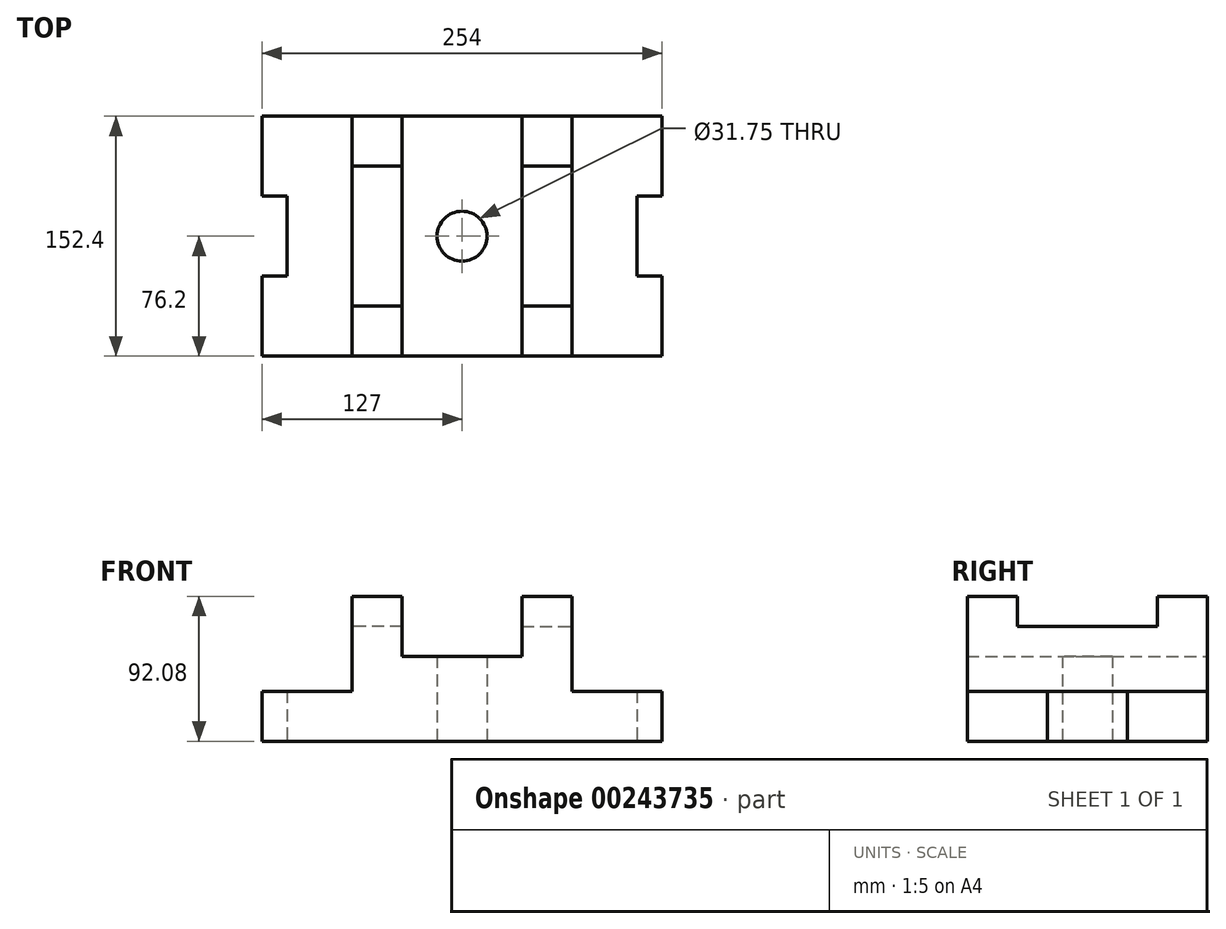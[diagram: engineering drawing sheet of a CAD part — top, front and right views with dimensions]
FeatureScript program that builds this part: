
annotation { "Feature Type Name" : "Feature", "Feature Type Description" : "" }
export const myFeature = defineFeature(function(context is Context, id is Id, definition is map)
    precondition{}
    {
        {
            var Q0;
            Q0=qCreatedBy(makeId("Top.planeOp"),FACE);
            var sketch = newSketch(context, id + "F0", { "sketchPlane" : qUnion([Q0])});
            skLineSegment(sketch, "E0", {"start": v(0, 0) * mm, "end": v(-127, 0) * mm});
            skLineSegment(sketch, "E1", {"start": v(0, 0) * mm, "end": v(0, 50.8) * mm});
            skLineSegment(sketch, "E2", {"start": v(-15.88, 50.8) * mm, "end": v(-15.88, 101.6) * mm});
            skLineSegment(sketch, "E3", {"start": v(-15.87, 101.6) * mm, "end": v(0, 101.6) * mm});
            skLineSegment(sketch, "E4", {"start": v(0, 50.8) * mm, "end": v(-15.88, 50.8) * mm});
            skLineSegment(sketch, "E5", {"start": v(0, 101.6) * mm, "end": v(0, 152.4) * mm});
            skLineSegment(sketch, "E6", {"start": v(0, 152.4) * mm, "end": v(-57.15, 152.4) * mm});
            skLineSegment(sketch, "E7", {"start": v(-57.15, 152.4) * mm, "end": v(-88.9, 152.4) * mm});
            skLineSegment(sketch, "E8", {"start": v(-88.9, 152.4) * mm, "end": v(-127, 152.4) * mm});
            skLineSegment(sketch, "E9", {"start": v(0, 0) * mm, "end": v(-57.15, 0) * mm});
            skLineSegment(sketch, "E10", {"start": v(-57.15, 152.4) * mm, "end": v(-57.15, 0) * mm});
            skLineSegment(sketch, "E11", {"start": v(-88.9, 120.65) * mm, "end": v(-57.15, 120.65) * mm});
            skLineSegment(sketch, "E12", {"start": v(-88.9, 0) * mm, "end": v(-88.9, 31.75) * mm});
            skLineSegment(sketch, "E13", {"start": v(-88.9, 31.75) * mm, "end": v(-57.15, 31.75) * mm});
            skLineSegment(sketch, "E14", {"start": v(-88.9, 152.4) * mm, "end": v(-88.9, 120.65) * mm});
            skLineSegment(sketch, "E15", {"start": v(-88.9, 120.65) * mm, "end": v(-88.9, 31.75) * mm});
            skLineSegment(sketch, "E16", {"start": v(-127, 152.4) * mm, "end": v(-127, 0) * mm});
            skLineSegment(sketch, "E17.MirrorCS", {"start": v(-165.1, 152.4) * mm, "end": v(-127, 152.4) * mm});
            skLineSegment(sketch, "E18.MirrorCS", {"start": v(-165.1, 152.4) * mm, "end": v(-165.1, 120.65) * mm});
            skLineSegment(sketch, "E19.MirrorCS", {"start": v(-196.85, 152.4) * mm, "end": v(-196.85, 0) * mm});
            skLineSegment(sketch, "E20.MirrorCS", {"start": v(-165.1, 120.65) * mm, "end": v(-165.1, 31.75) * mm});
            skLineSegment(sketch, "E21.MirrorCS", {"start": v(-254, 0) * mm, "end": v(-127, 0) * mm});
            skLineSegment(sketch, "E22.MirrorCS", {"start": v(-165.1, 0) * mm, "end": v(-165.1, 31.75) * mm});
            skLineSegment(sketch, "E23.MirrorCS", {"start": v(-196.85, 152.4) * mm, "end": v(-165.1, 152.4) * mm});
            skLineSegment(sketch, "E24.MirrorCS", {"start": v(-254, 152.4) * mm, "end": v(-196.85, 152.4) * mm});
            skLineSegment(sketch, "E25.MirrorCS", {"start": v(-254, 101.6) * mm, "end": v(-254, 152.4) * mm});
            skLineSegment(sketch, "E26.MirrorCS", {"start": v(-238.12, 50.8) * mm, "end": v(-238.12, 101.6) * mm});
            skLineSegment(sketch, "E27.MirrorCS", {"start": v(-254, 50.8) * mm, "end": v(-238.12, 50.8) * mm});
            skLineSegment(sketch, "E28.MirrorCS", {"start": v(-238.13, 101.6) * mm, "end": v(-254, 101.6) * mm});
            skLineSegment(sketch, "E29.MirrorCS", {"start": v(-254, 0) * mm, "end": v(-254, 50.8) * mm});
            skLineSegment(sketch, "E30.MirrorCS", {"start": v(-165.1, 120.65) * mm, "end": v(-196.85, 120.65) * mm});
            skLineSegment(sketch, "E31.MirrorCS", {"start": v(-165.1, 31.75) * mm, "end": v(-196.85, 31.75) * mm});
            skCircle(sketch, "E32", {"center": v(-127, 76.2) * mm, "radius": 15.88 * mm});
            skSolve(sketch);
        }
        {
            var Q0;
            Q0=makeQuery(id+"F0.imprint","IMPRINT",FACE,{"disambiguationData":[TD([[makeQuery(id+"F0.imprint","IMPRINT",EDGE,{"derivedFrom":sQuery(id+"F0.wireOp",EDGE,"E1")}),1.0]])]});
            extrude(context, id + "F1", {"entities" : qUnion([Q0]), "depth" : 31.75 * mm});
        }
        {
            var Q0;
            {var subQ0=sQuery(id+"F0.wireOp",EDGE,"E7");Q0=makeQuery(id+"F0.imprint","IMPRINT",FACE,{"disambiguationData":[TD([[makeQuery(id+"F0.imprint","IMPRINT",EDGE,{"derivedFrom":subQ0}),1.0]])]});}
            var Q1;
            {var subQ3=sQuery(id+"F0.wireOp",EDGE,"E12");Q1=makeQuery(id+"F0.imprint","IMPRINT",FACE,{"disambiguationData":[TD([[makeQuery(id+"F0.imprint","IMPRINT",EDGE,{"derivedFrom":subQ3}),-1.0]])]});}
            extrude(context, id + "F2", {"entities" : qUnion([Q0, Q1]), "operationType" : NewBodyOperationType.ADD, "depth" : 92.07 * mm});
        }
        {
            var Q0;
            {var subQ0=sQuery(id+"F0.wireOp",EDGE,"E11");Q0=makeQuery(id+"F0.imprint","IMPRINT",FACE,{"disambiguationData":[TD([[makeQuery(id+"F0.imprint","IMPRINT",EDGE,{"derivedFrom":subQ0}),-1.0]])]});}
            extrude(context, id + "F3", {"entities" : qUnion([Q0]), "operationType" : NewBodyOperationType.ADD, "depth" : 73.02 * mm});
        }
        {
            var Q0;
            Q0=makeQuery(id+"F0.imprint","IMPRINT",FACE,{"disambiguationData":[TD([[makeQuery(id+"F0.imprint","IMPRINT",EDGE,{"derivedFrom":sQuery(id+"F0.wireOp",EDGE,"E8")}),1.0]])]});
            extrude(context, id + "F4", {"entities" : qUnion([Q0]), "operationType" : NewBodyOperationType.ADD, "depth" : 53.97 * mm});
        }
        {
            var Q0;
            {var subQ1=sQuery(id+"F0.wireOp",EDGE,"E16");Q0=makeQuery(id+"F0.imprint","IMPRINT",FACE,{"disambiguationData":[TD([[makeQuery(id+"F0.imprint","IMPRINT",EDGE,{"derivedFrom":subQ1}),-1.0]])]});}
            extrude(context, id + "F5", {"entities" : qUnion([Q0]), "operationType" : NewBodyOperationType.ADD, "depth" : 53.97 * mm});
        }
        {
            var Q0;
            Q0=makeQuery(id+"F0.imprint","IMPRINT",FACE,{"disambiguationData":[TD([[makeQuery(id+"F0.imprint","IMPRINT",EDGE,{"derivedFrom":sQuery(id+"F0.wireOp",EDGE,"E18.MirrorCS")}),-1.0]])]});
            var Q1;
            {var subQ0=sQuery(id+"F0.wireOp",EDGE,"E31.MirrorCS");Q1=makeQuery(id+"F0.imprint","IMPRINT",FACE,{"disambiguationData":[TD([[makeQuery(id+"F0.imprint","IMPRINT",EDGE,{"derivedFrom":subQ0}),1.0]])]});}
            extrude(context, id + "F6", {"entities" : qUnion([Q0, Q1]), "operationType" : NewBodyOperationType.ADD, "depth" : 92.07 * mm});
        }
        {
            var Q0;
            Q0=makeQuery(id+"F0.imprint","IMPRINT",FACE,{"disambiguationData":[TD([[makeQuery(id+"F0.imprint","IMPRINT",EDGE,{"derivedFrom":sQuery(id+"F0.wireOp",EDGE,"E20.MirrorCS")}),-1.0]])]});
            extrude(context, id + "F7", {"entities" : qUnion([Q0]), "operationType" : NewBodyOperationType.ADD, "depth" : 73.02 * mm});
        }
        {
            var Q0;
            {var subQ5=sQuery(id+"F0.wireOp",EDGE,"E24.MirrorCS");Q0=makeQuery(id+"F0.imprint","IMPRINT",FACE,{"disambiguationData":[TD([[makeQuery(id+"F0.imprint","IMPRINT",EDGE,{"derivedFrom":subQ5}),-1.0]])]});}
            extrude(context, id + "F8", {"entities" : qUnion([Q0]), "operationType" : NewBodyOperationType.ADD, "depth" : 31.75 * mm});
        }
    });
